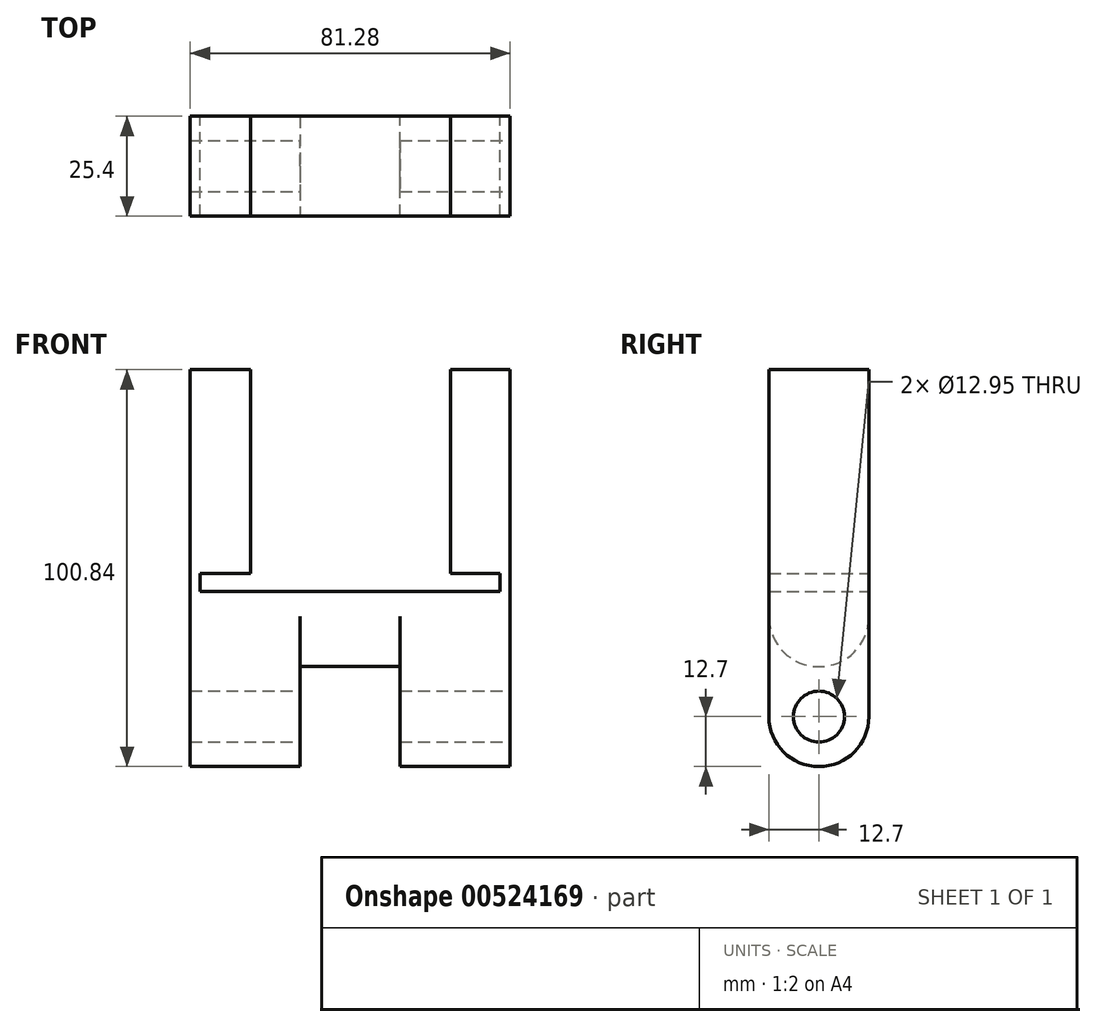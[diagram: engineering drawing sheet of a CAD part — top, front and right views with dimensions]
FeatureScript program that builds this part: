
annotation { "Feature Type Name" : "Feature", "Feature Type Description" : "" }
export const myFeature = defineFeature(function(context is Context, id is Id, definition is map)
    precondition{}
    {
        {
            var Q0;
            Q0=qCreatedBy(makeId("Front.planeOp"),FACE);
            var sketch = newSketch(context, id + "F0", { "sketchPlane" : qUnion([Q0])});
            skLineSegment(sketch, "E0", {"start": v(-12.7, 0) * mm, "end": v(-12.7, 25.4) * mm});
            skLineSegment(sketch, "E1", {"start": v(-12.7, 25.4) * mm, "end": v(12.7, 25.4) * mm});
            skLineSegment(sketch, "E2", {"start": v(12.7, 25.4) * mm, "end": v(12.7, 0) * mm});
            skLineSegment(sketch, "E3", {"start": v(12.7, 0) * mm, "end": v(40.64, 0) * mm});
            skLineSegment(sketch, "E4", {"start": v(40.64, 0) * mm, "end": v(40.64, 44.45) * mm});
            skLineSegment(sketch, "E5", {"start": v(40.64, 44.45) * mm, "end": v(-40.64, 44.45) * mm});
            skLineSegment(sketch, "E6", {"start": v(-40.64, 44.45) * mm, "end": v(-40.64, 0) * mm});
            skLineSegment(sketch, "E7", {"start": v(-40.64, 0) * mm, "end": v(-12.7, 0) * mm});
            skLineSegment(sketch, "E8", {"start": v(-38.1, 44.45) * mm, "end": v(-38.1, 49.11) * mm});
            skLineSegment(sketch, "E9", {"start": v(38.1, 44.45) * mm, "end": v(38.1, 49.11) * mm});
            skLineSegment(sketch, "E10", {"start": v(-38.1, 49.11) * mm, "end": v(-25.34, 49.11) * mm});
            skLineSegment(sketch, "E11", {"start": v(38.1, 49.11) * mm, "end": v(25.46, 49.11) * mm});
            skLineSegment(sketch, "E12", {"start": v(-38.1, 100.84) * mm, "end": v(38.1, 100.84) * mm});
            skLineSegment(sketch, "E13", {"start": v(25.46, 49.11) * mm, "end": v(25.46, 100.84) * mm});
            skLineSegment(sketch, "E14", {"start": v(-25.34, 49.11) * mm, "end": v(-25.34, 100.84) * mm});
            skLineSegment(sketch, "E15", {"start": v(-38.1, 100.84) * mm, "end": v(-40.64, 100.84) * mm});
            skLineSegment(sketch, "E16", {"start": v(-40.64, 100.84) * mm, "end": v(-40.64, 44.45) * mm});
            skLineSegment(sketch, "E17", {"start": v(40.64, 44.45) * mm, "end": v(40.64, 100.84) * mm});
            skLineSegment(sketch, "E18", {"start": v(40.64, 100.84) * mm, "end": v(38.1, 100.84) * mm});
            skSolve(sketch);
        }
        {
            var Q0;
            Q0=makeQuery(id+"F0.imprint","IMPRINT",FACE,{"disambiguationData":[TD([[makeQuery(id+"F0.imprint","IMPRINT",EDGE,{"derivedFrom":sQuery(id+"F0.wireOp",EDGE,"E0")}),1.0]])]});
            var Q1;
            {var subQ5=sQuery(id+"F0.wireOp",EDGE,"E8");Q1=makeQuery(id+"F0.imprint","IMPRINT",FACE,{"disambiguationData":[TD([[makeQuery(id+"F0.imprint","IMPRINT",EDGE,{"derivedFrom":subQ5}),1.0]])]});}
            var Q2;
            {var subQ5=sQuery(id+"F0.wireOp",EDGE,"E9");Q2=makeQuery(id+"F0.imprint","IMPRINT",FACE,{"disambiguationData":[TD([[makeQuery(id+"F0.imprint","IMPRINT",EDGE,{"derivedFrom":subQ5}),-1.0]])]});}
            extrude(context, id + "F1", {"entities" : qUnion([Q0, Q1, Q2]), "endBound" : BoundingType.SYMMETRIC, "depth" : 25.4 * mm});
        }
        {
            var Q0;
            Q0=qCreatedBy(makeId("Right.planeOp"),FACE);
            var sketch = newSketch(context, id + "F2", { "sketchPlane" : qUnion([Q0])});
            skArc(sketch, "E19", {"start": v(-12.7, 38.1) * mm, "mid": v(0, 25.4) * mm, "end": v(12.7, 38.1) * mm});
            skLineSegment(sketch, "E20", {"start": v(-12.7, 38.1) * mm, "end": v(-12.7, 24.45) * mm});
            skLineSegment(sketch, "E21", {"start": v(-12.7, 24.45) * mm, "end": v(12.7, 24.45) * mm});
            skLineSegment(sketch, "E22", {"start": v(12.7, 24.45) * mm, "end": v(12.7, 38.1) * mm});
            skSolve(sketch);
        }
        {
            var Q0;
            Q0=qSketchRegion(id+"F2",true);
            extrude(context, id + "F3", {"entities" : qUnion([Q0]), "operationType" : NewBodyOperationType.REMOVE, "endBound" : BoundingType.SYMMETRIC, "depth" : 25.4 * mm});
        }
        {
            var Q0;
            Q0=makeQuery(id+"F1.opExtrude","SWEPT_FACE",FACE,{"disambiguationData":[OSD([sQuery(id+"F0.wireOp",EDGE,"E4")])]});
            var sketch = newSketch(context, id + "F4", { "sketchPlane" : qUnion([Q0])});
            skArc(sketch, "E23", {"start": v(-12.7, 12.7) * mm, "mid": v(0, 0) * mm, "end": v(12.7, 12.7) * mm});
            skPoint(sketch, "E23.centerSnap0", {"position": v(0, 0) * mm});
            skLineSegment(sketch, "E24", {"start": v(-12.7, 12.7) * mm, "end": v(-12.7, 0) * mm});
            skLineSegment(sketch, "E25", {"start": v(-12.7, 0) * mm, "end": v(12.7, 0) * mm});
            skLineSegment(sketch, "E26", {"start": v(12.7, 0) * mm, "end": v(12.7, 12.7) * mm});
            skCircle(sketch, "E27", {"center": v(0, 12.7) * mm, "radius": 6.48 * mm});
            skSolve(sketch);
        }
        {
            var Q0;
            Q0=qSketchRegion(id+"F4",true);
            extrude(context, id + "F5", {"entities" : qUnion([Q0]), "operationType" : NewBodyOperationType.REMOVE, "endBound" : BoundingType.THROUGH_ALL, "oppositeDirection" : true, "depth" : 25.4 * mm});
        }
    });
